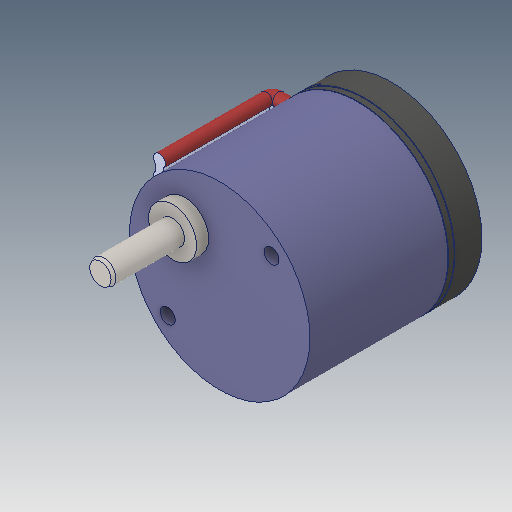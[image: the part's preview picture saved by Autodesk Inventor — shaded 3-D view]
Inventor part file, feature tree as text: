
AUTODESK INVENTOR PART (.ipt)
format: ipt  version: 2019 (Build 230136000, 136)  size: 222,208 bytes
history: native  units: mm
features: imported_body x1, sweep x1
ambient origin geometry x8: Origin, YZ Plane, XZ Plane, XY Plane, X Axis, Y Axis, Z Axis, Center Point
bodies: Solid1 (feature_tree), Solid2 (feature_tree)
feature tree (2):
  imported_body  "Imported1"
  sweep  "Sweep1"
